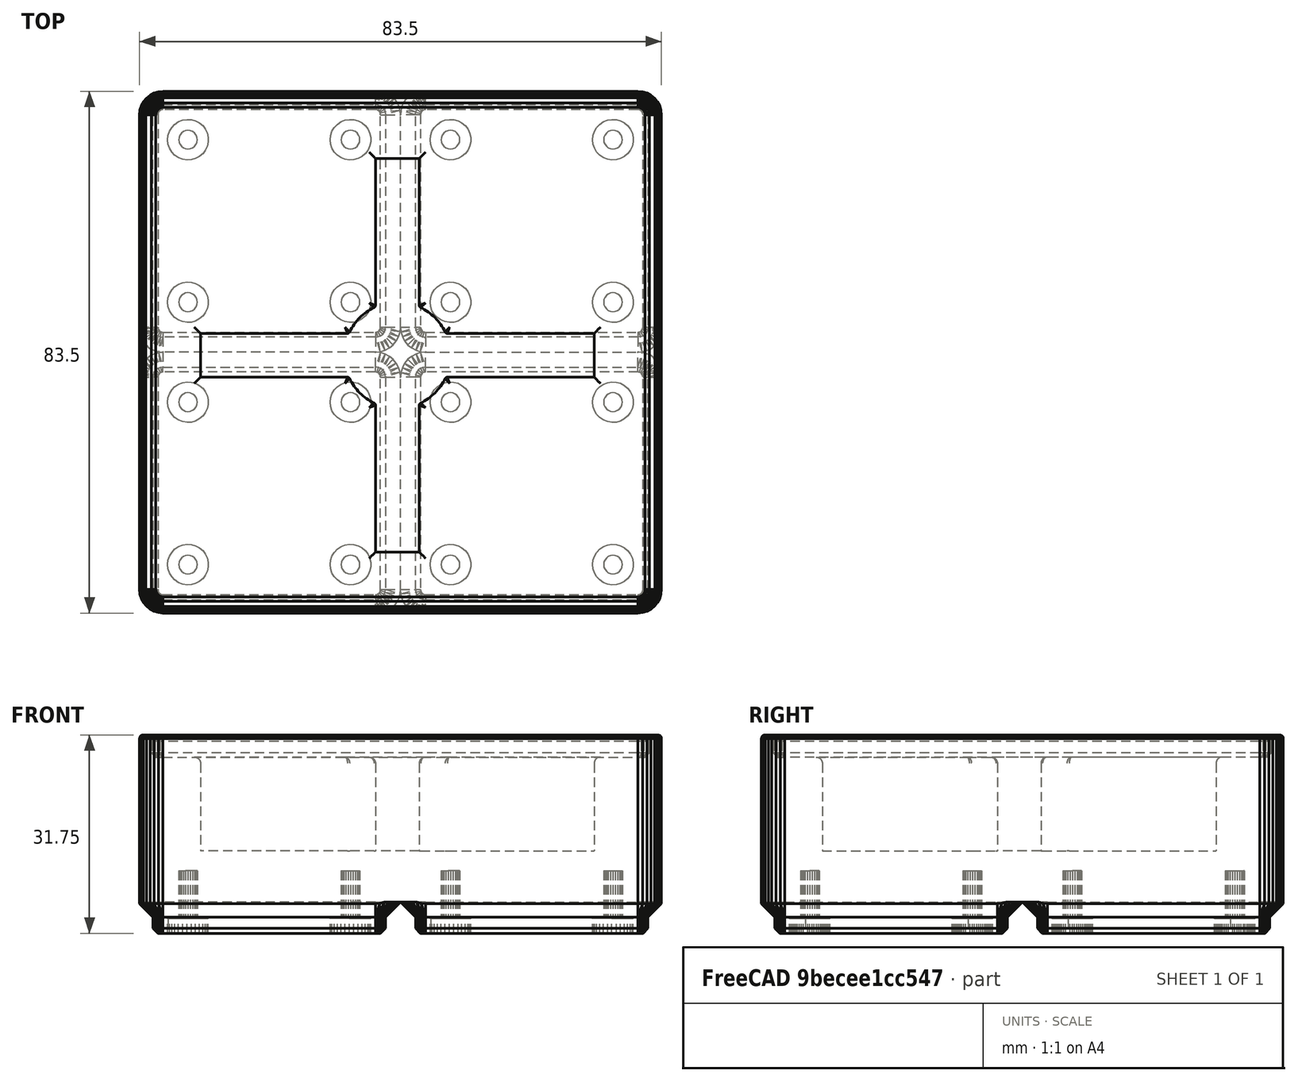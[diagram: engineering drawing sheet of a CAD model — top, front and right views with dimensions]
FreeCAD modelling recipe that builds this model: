
FCSTD DOCUMENT  (FreeCAD 0.20R29410 (Git))
Label: 2x2_giottos_gtaa1900_super_rocket_air_blower
License: All rights reserved
LicenseURL: http://en.wikipedia.org/wiki/All_rights_reserved
objects: Part::Feature×2, PartDesign::Fillet×2, Mesh::Feature×1, Part::Refine×1, PartDesign::FeatureBase×1, Sketcher::SketchObject×1, PartDesign::Pocket×1, PartDesign::Body×1
note: 12 computed .brp shape members not serialized (recipe doc carries the construction recipe); baked Part::Feature solids carry a one-line shape summary decoded from their .brp

FEATURE [Mesh::Feature] _x2_Block_1_25in  label="2x2 Block 1.25in"
FEATURE [Part::Feature] _x2_Block_1_25in001
  shape: bbox 83.5 x 83.5 x 31.75 mm, 6748 faces, 0 solids (baked)
FEATURE [Part::Refine] _x2_Block_1_25in001001
  Source = -> _x2_Block_1_25in001
FEATURE [Part::Feature] _x2_Block_1_25in001001_solid  label="_x2_Block_1_25in001001 (Solid)"
  shape: bbox 83.5 x 83.5 x 31.75 mm, 2184 faces (baked)
FEATURE [PartDesign::FeatureBase] BaseFeature
  BaseFeature = -> _x2_Block_1_25in001001_solid
FEATURE [Sketcher::SketchObject] Sketch
  FullyConstrained = true
  MapMode = 5
  Placement = pos=(0,0,28.2005) rot=(0,0,1;0rad)
  Support = -> [BaseFeature]
  expr: Constraints[22] = (2 * 41.5 - 63) / 2
  expr: Constraints[23] = (41.5 * 2 - 63) / 2
  sketch-geometry (16):
    g0: LineSegment StartX=38 StartY=10 StartZ=0 EndX=45 EndY=10 EndZ=0
    g1: LineSegment StartX=45 StartY=10 StartZ=0 EndX=45 EndY=33.754 EndZ=0
    g2: LineSegment StartX=49.246 StartY=38 StartZ=0 EndX=73 EndY=38 EndZ=0
    g3: LineSegment StartX=73 StartY=38 StartZ=0 EndX=73 EndY=45 EndZ=0
    g4: LineSegment StartX=73 StartY=45 StartZ=0 EndX=49.246 EndY=45 EndZ=0
    g5: LineSegment StartX=45 StartY=49.246 StartZ=0 EndX=45 EndY=73 EndZ=0
    g6: LineSegment StartX=45 StartY=73 StartZ=0 EndX=38 EndY=73 EndZ=0
    g7: LineSegment StartX=38 StartY=73 StartZ=0 EndX=38 EndY=49.246 EndZ=0
    g8: LineSegment StartX=33.754 StartY=45 StartZ=0 EndX=10 EndY=45 EndZ=0
    g9: LineSegment StartX=10 StartY=45 StartZ=0 EndX=10 EndY=38 EndZ=0
    g10: LineSegment StartX=10 StartY=38 StartZ=0 EndX=33.754 EndY=38 EndZ=0
    g11: LineSegment StartX=38 StartY=33.754 StartZ=0 EndX=38 EndY=10 EndZ=0
    g12: ArcOfCircle CenterX=41.5 CenterY=41.5 CenterZ=0 NormalX=0 NormalY=0 NormalZ=1 AngleXU=0 Radius=8.5 StartAngle=5.13678 EndAngle=5.8588
    g13: ArcOfCircle CenterX=41.5 CenterY=41.5 CenterZ=0 NormalX=0 NormalY=0 NormalZ=1 AngleXU=0 Radius=8.5 StartAngle=0.42439 EndAngle=1.14641
    g14: ArcOfCircle CenterX=41.5 CenterY=41.5 CenterZ=0 NormalX=0 NormalY=0 NormalZ=1 AngleXU=0 Radius=8.5 StartAngle=1.99519 EndAngle=2.7172
    g15: ArcOfCircle CenterX=41.5 CenterY=41.5 CenterZ=0 NormalX=0 NormalY=0 NormalZ=1 AngleXU=0 Radius=8.5 StartAngle=3.56598 EndAngle=4.288
  constraints (53):
    c: Horizontal(g0)
    c: Coincident(g0,g1)
    c: Vertical(g1)
    c: Horizontal(g2)
    c: Coincident(g2,g3)
    c: Vertical(g3)
    c: Coincident(g3,g4)
    c: Horizontal(g4)
    c: Vertical(g5)
    c: Coincident(g5,g6)
    c: Horizontal(g6)
    c: Coincident(g6,g7)
    c: Vertical(g7)
    c: Horizontal(g8)
    c: Coincident(g8,g9)
    c: Vertical(g9)
    c: Coincident(g9,g10)
    c: Horizontal(g10)
    c: Coincident(g11,g0)
    c: Vertical(g11)
    c: Equal(g9,g0)
    c: DistanceX(g8,g3) = 63
    c: DistanceX(g-1,g9) = 10
    c: DistanceY(g-1,g0) = 10
    c: DistanceY(g3,g3) = 7
    c: Diameter(g12) = 17
    c: DistanceX(g-1,g12) = 41.5
    c: DistanceY(g-1,g12) = 41.5
    c: PointOnObject(g7,g12)
    c: PointOnObject(g8,g12)
    c: PointOnObject(g5,g12)
    c: PointOnObject(g10,g12)
    c: Coincident(g15,g11)
    c: Coincident(g12,g1)
    c: Equal(g12,g13)
    c: Coincident(g12,g2)
    c: Coincident(g13,g4)
    c: Coincident(g12,g13)
    c: Equal(g13,g14)
    c: PointOnObject(g13,g5)
    c: PointOnObject(g14,g7)
    c: Coincident(g13,g14)
    c: Equal(g14,g15)
    c: PointOnObject(g14,g8)
    c: PointOnObject(g15,g10)
    c: Coincident(g14,g15)
    c: DistanceX(g0,g0) = 7
    c: DistanceX(g6,g6) = 7
    c: Vertical(g4,g2)
    c: Vertical(g10,g8)
    c: Horizontal(g11,g1)
    c: Horizontal(g7,g5)
    c: Equal(g4,g5)
FEATURE [PartDesign::Pocket] Pocket
  BaseFeature = -> BaseFeature
  Direction = (0,0,-1)
  Length = 15
  Length2 = 5
  Profile = -> Sketch
  ReferenceAxis = -> Sketch [N_Axis]
  Type = 0
FEATURE [PartDesign::Fillet] Fillet
  Base = -> Pocket [Edge4362,Edge4363,Edge4364,Edge4361,Edge4360,Edge4359,Edge4358,Edge4357,Edge4356,Edge4355,Edge4354,Edge4353,Edge4352,Edge4351,Edge4366,Edge4365]
  BaseFeature = -> Pocket
  Radius = 1
  SupportTransform = false
  UseAllEdges = false
FEATURE [PartDesign::Fillet] Fillet001
  Base = -> Fillet [Edge143,Edge147,Edge133,Edge136,Edge159,Edge163,Edge152,Edge148]
  BaseFeature = -> Fillet
  Radius = 0.4
  SupportTransform = false
  UseAllEdges = false
FEATURE [PartDesign::Body] Body
  BaseFeature = -> _x2_Block_1_25in001001_solid
  Group = -> [BaseFeature,Sketch,Pocket,Fillet,Fillet001]
  Origin = -> Origin
  Tip = -> Fillet001
